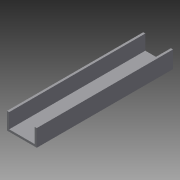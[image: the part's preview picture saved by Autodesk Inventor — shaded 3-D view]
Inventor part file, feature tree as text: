
AUTODESK INVENTOR PART (.ipt)
format: ipt  version: 2015 (Build 190159000, 159)  size: 75,264 bytes
history: native  units: in
note: dims shown in document units (in); Inventor stores cm internally (conversion verified against a paired STEP export)
features: extrude x1, sketch x1
ambient origin geometry x8: Origin, YZ Plane, XZ Plane, XY Plane, X Axis, Y Axis, Z Axis, Center Point
bodies: Solid1 (feature_tree)
feature tree (2):
  extrude  "Extrusion1"  Depth=1.0in
  sketch  "Sketch1"  dims[d0=1.75in d1=1.0in d2=0.125in d3=8.0in d4=0.0in]
